# Revit family: Anti_Siphon_Sillcock-JayR.Smith-567X_Series
name_source: partatom
category: Plumbing Fixtures
units: mm (PartAtom-declared; Revit-internal decimal feet)

## family parameters
Cut with Voids When Loaded = No
Host = Face
OmniClass Number = 23.45.55.14
OmniClass Title = Single Faucets
Part Type = Normal
Room Calculation Point = No
Round Connector Dimension = Use Diameter
Shared = No

## types (2) — shared parameters
-CP Rough Chrome Plated = No
Assembly Code = D2020300
Body Material = Metal-JayR.Smith-Cast Brass
CW Connection = Yes
Default Elevation = 0"
Description = Mild Climate Anti-Siphon Sillcock
HW Connection = No
Handle Material = Aluminum-JayR.Smith-Powder Coated
Height = 4"
Hose Connection  Size = 3/4"
Hose Connection Description = 3/4" Hose Outlet Connection
Inlet Size = 1"
Installation Type = Wall Mounted
Length = 3"
Manufacturer = JayR.Smith
Operator Type = Handle
Product Documentation Link = https://www.jrsmith.com
Product Page URL = https://www.jrsmith.com
URL = https://www.jrsmith.com
Vent Connection = No
Waste Connection = No
Width = 2"

## per-type parameters (varying)
| type | Inlet Connection Description | Inlet Radius |
| 5672 | 1/2" Female NPT Inlet Connection | 1/4" |
| 5673 | 3/4" Female NPT Inlet Connection | 3/8" |

note: column(s) folded — value = type name in every type: Model

## geometry (parser evidence)
native form markers: Sweep x2
no freeform markers — native parametric forms only
